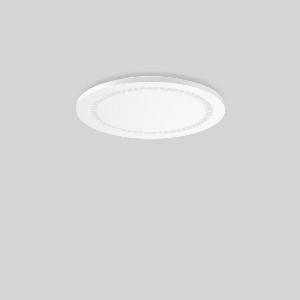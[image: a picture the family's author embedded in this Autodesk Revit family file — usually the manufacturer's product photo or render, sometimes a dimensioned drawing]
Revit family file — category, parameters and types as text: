
# Revit family: hemis_round_312186_002_3_2615
name_source: partatom
category: Lighting Fixtures
units: mm (PartAtom-declared; Revit-internal decimal feet)

## family parameters
Cut with Voids When Loaded = No
Host = Face
Light Source = No
Part Type = Normal
Room Calculation Point = No
Round Connector Dimension = Use Diameter
Shared = No

## types (1)
- MultiLumen 1 (1 x LED Modul 840, 3350 lm, 4000)
    Apparent Load = 25 VA
    CIE Flux Codes = 85 98 100 100 100
    Color Rendering = 80
    Color Temperature = 4000
    Default Elevation = 1800 mm
    Description = Series: HEMIS round
Glare-free LED ceiling luminaire with optical lens system. Base: metal, powder-coated, with bayonet fixing. Housing: plastic (polycarbonate). Housing and diffuser are screwed together. Diffuser with optic lenses. Big terminal block; ideal for through-wiring. Sealing strip on the back of the luminaire connects seamlessly with the ceiling. Easy installation with Plug+Play plug connection. Thanks to RUG < 22 ideal for corridors, stairways, shops, schools, meeting rooms, rest areas. 
Colour: white
Diameter: 400 mm
Height: 33 mm
Lamp: LED
Socket: without socket
Colour temperature: 4000K
Colour rendering index (CRI): 80
System power: 25 W
Rated luminous flux: 3350 lm
Luminous efficiency: 134 lm/W
System power 2: 22 W
Rated luminous flux 2: 2850 lm
Luminous efficiency 2: 130 lm/W
Control gear: Regulated power supply
Protection class: I
Type of protection: IP 40
    Height = 33 mm
    Lamp = 1 x LED Modul 840
    Lamp Light Flux = 3350 lm
    Lamp count = 1
    Length = 400 mm
    Lifetime = 50000 h
    Luminous efficacy = 134 lm/W
    Manufacturer = RZB
    ModVariant = No
    Model = 312186.002.3
    Mounting Place = Ceiling
    Mounting Type = Surface mounted
    Number of Poles = 1
    OnlyDefault = Yes
    Power Factor = 1
    Product Name = HEMIS round
    Product group = Surface mounted modular luminaires
    ProductGroupID = 306
    Protection Class = Protection class I
    Protection Degree = Degree of protection
    RLX_Detail_Level = 1
    RLX_Emergency_Light_Flux = 0 lm
    RLX_Emergency_Type = 0
    RLX_Emergency_Type_DB = No
    RlxData = <blob elided: 41293 chars, md5=cb3e900c>
    Socket = socket
    Standby Power = 0 W
    System Light Flux = 3350 lm
    System Power = 25 W
    Type Comments = MultiLumen 1
    Type Image = 312186.002.jpg
    URL = http://relux.com
    VarID = multilumen_1
    Voltage = 0 V
    Weight = 0.00 kg
    Width = 0 mm  [stored 0 ft]

note: [stored X ft] marks values corroborated as IEEE doubles in the binary element streams (Revit-internal decimal feet)

## geometry (parser evidence)
native form markers: Blend x4, Sweep x10
no freeform markers — native parametric forms only
